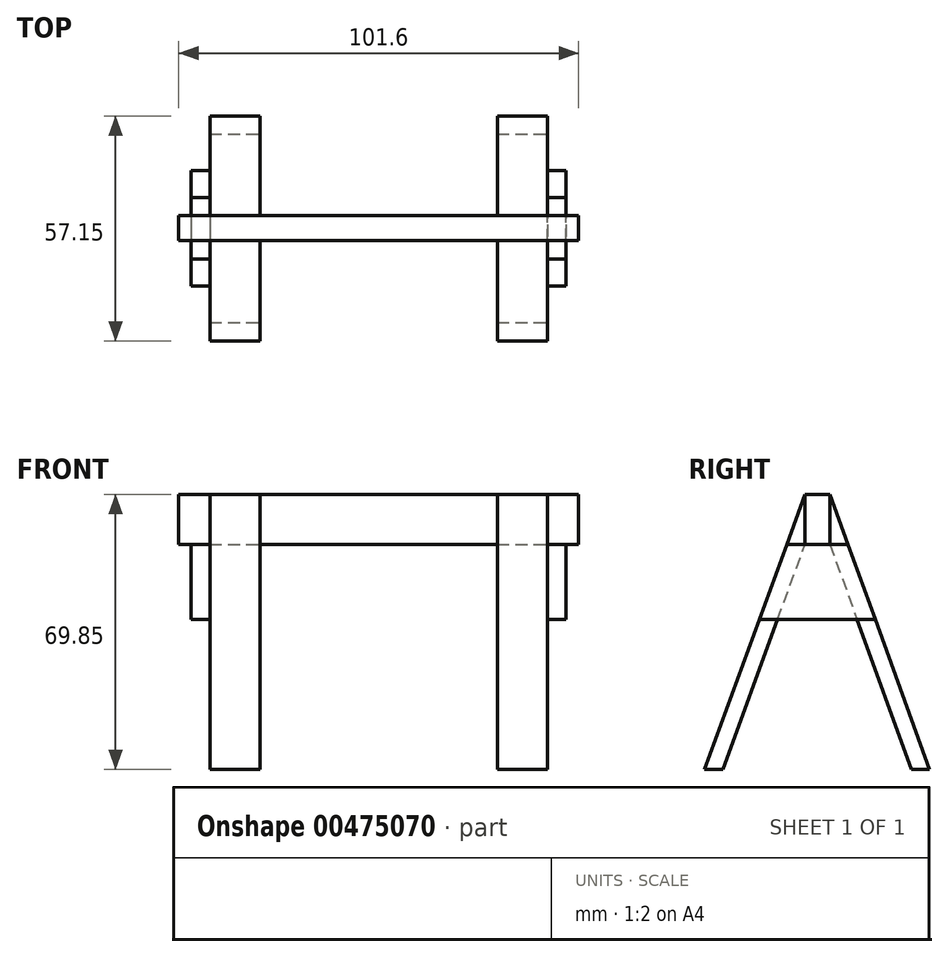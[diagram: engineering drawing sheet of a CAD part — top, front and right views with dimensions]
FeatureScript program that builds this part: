
annotation { "Feature Type Name" : "Feature", "Feature Type Description" : "" }
export const myFeature = defineFeature(function(context is Context, id is Id, definition is map)
    precondition{}
    {
        {
            var Q0;
            Q0=qCreatedBy(makeId("Right.planeOp"),FACE);
            var sketch = newSketch(context, id + "F0", { "sketchPlane" : qUnion([Q0])});
            skLineSegment(sketch, "E0.bottom", {"start": v(-4.7, 33.69) * mm, "end": v(1.65, 33.69) * mm});
            skLineSegment(sketch, "E0.top", {"start": v(-4.7, 20.99) * mm, "end": v(1.65, 20.99) * mm});
            skLineSegment(sketch, "E0.left", {"start": v(-4.7, 33.69) * mm, "end": v(-4.7, 20.99) * mm});
            skLineSegment(sketch, "E0.right", {"start": v(1.65, 33.69) * mm, "end": v(1.65, 20.99) * mm});
            skLineSegment(sketch, "E1", {"start": v(-4.7, 33.69) * mm, "end": v(-30.2, -36.16) * mm});
            skLineSegment(sketch, "E2", {"start": v(-25.57, -36.16) * mm, "end": v(-4.7, 20.99) * mm});
            skLineSegment(sketch, "E3", {"start": v(-30.2, -36.16) * mm, "end": v(-25.57, -36.16) * mm});
            skLineSegment(sketch, "E4", {"start": v(22.34, -36.16) * mm, "end": v(26.94, -36.16) * mm});
            skLineSegment(sketch, "E5", {"start": v(1.65, 20.99) * mm, "end": v(22.34, -36.16) * mm});
            skLineSegment(sketch, "E6", {"start": v(1.65, 33.69) * mm, "end": v(26.94, -36.16) * mm});
            skLineSegment(sketch, "E7", {"start": v(-4.7, 20.99) * mm, "end": v(-9.33, 20.99) * mm});
            skLineSegment(sketch, "E8", {"start": v(1.65, 20.99) * mm, "end": v(6.25, 20.99) * mm});
            skLineSegment(sketch, "E9", {"start": v(6.2, 1.92) * mm, "end": v(13.16, 1.92) * mm});
            skLineSegment(sketch, "E10", {"start": v(6.2, 1.92) * mm, "end": v(-16.3, 1.92) * mm});
            skLineSegment(sketch, "E11", {"start": v(-9.33, 20.99) * mm, "end": v(-16.3, 1.92) * mm});
            skLineSegment(sketch, "E12", {"start": v(6.25, 20.99) * mm, "end": v(13.16, 1.92) * mm});
            skSolve(sketch);
        }
        {
            var Q0;
            Q0=makeQuery(id+"F0.imprint","IMPRINT",FACE,{"disambiguationData":[TD([[makeQuery(id+"F0.imprint","IMPRINT",EDGE,{"derivedFrom":sQuery(id+"F0.wireOp",EDGE,"E0.bottom")}),-1.0]])]});
            extrude(context, id + "F1", {"entities" : qUnion([Q0]), "oppositeDirection" : true, "depth" : 101.6 * mm});
        }
        {
            var Q0;
            {var subQ0=sQuery(id+"F0.wireOp",EDGE,"E3");Q0=makeQuery(id+"F0.imprint","IMPRINT",FACE,{"disambiguationData":[TD([[makeQuery(id+"F0.imprint","IMPRINT",EDGE,{"derivedFrom":subQ0}),1.0]])]});}
            var Q1;
            {var subQ0=sQuery(id+"F0.wireOp",EDGE,"E4");Q1=makeQuery(id+"F0.imprint","IMPRINT",FACE,{"disambiguationData":[TD([[makeQuery(id+"F0.imprint","IMPRINT",EDGE,{"derivedFrom":subQ0}),1.0]])]});}
            var Q2;
            {var subQ0=sQuery(id+"F0.wireOp",EDGE,"E0.left");Q2=makeQuery(id+"F0.imprint","IMPRINT",FACE,{"disambiguationData":[TD([[makeQuery(id+"F0.imprint","IMPRINT",EDGE,{"derivedFrom":subQ0}),-1.0]])]});}
            var Q3;
            {var subQ0=sQuery(id+"F0.wireOp",EDGE,"E0.right");Q3=makeQuery(id+"F0.imprint","IMPRINT",FACE,{"disambiguationData":[TD([[makeQuery(id+"F0.imprint","IMPRINT",EDGE,{"derivedFrom":subQ0}),1.0]])]});}
            var Q4;
            Q4=makeQuery(id+"F0.imprint","IMPRINT",FACE,{"disambiguationData":[TD([[makeQuery(id+"F0.imprint","IMPRINT",EDGE,{"derivedFrom":sQuery(id+"F0.wireOp",EDGE,"E0.bottom")}),-1.0]])]});
            var Q5;
            {var subQ0=sQuery(id+"F0.wireOp",EDGE,"E7");Q5=makeQuery(id+"F0.imprint","IMPRINT",FACE,{"disambiguationData":[TD([[makeQuery(id+"F0.imprint","IMPRINT",EDGE,{"derivedFrom":subQ0}),1.0]])]});}
            var Q6;
            {var subQ0=sQuery(id+"F0.wireOp",EDGE,"E8");Q6=makeQuery(id+"F0.imprint","IMPRINT",FACE,{"disambiguationData":[TD([[makeQuery(id+"F0.imprint","IMPRINT",EDGE,{"derivedFrom":subQ0}),-1.0]])]});}
            extrude(context, id + "F2", {"entities" : qUnion([Q0, Q1, Q2, Q3, Q4, Q5, Q6]), "operationType" : NewBodyOperationType.ADD, "oppositeDirection" : true, "depth" : 20.64 * mm, "hasSecondDirection" : true, "secondDirectionOppositeDirection" : true, "secondDirectionDepth" : 7.94 * mm});
        }
        {
            var Q0;
            {var subQ0=sQuery(id+"F0.wireOp",EDGE,"E3");Q0=makeQuery(id+"F0.imprint","IMPRINT",FACE,{"disambiguationData":[TD([[makeQuery(id+"F0.imprint","IMPRINT",EDGE,{"derivedFrom":subQ0}),1.0]])]});}
            var Q1;
            {var subQ0=sQuery(id+"F0.wireOp",EDGE,"E4");Q1=makeQuery(id+"F0.imprint","IMPRINT",FACE,{"disambiguationData":[TD([[makeQuery(id+"F0.imprint","IMPRINT",EDGE,{"derivedFrom":subQ0}),1.0]])]});}
            var Q2;
            {var subQ0=sQuery(id+"F0.wireOp",EDGE,"E8");Q2=makeQuery(id+"F0.imprint","IMPRINT",FACE,{"disambiguationData":[TD([[makeQuery(id+"F0.imprint","IMPRINT",EDGE,{"derivedFrom":subQ0}),-1.0]])]});}
            var Q3;
            {var subQ0=sQuery(id+"F0.wireOp",EDGE,"E7");Q3=makeQuery(id+"F0.imprint","IMPRINT",FACE,{"disambiguationData":[TD([[makeQuery(id+"F0.imprint","IMPRINT",EDGE,{"derivedFrom":subQ0}),1.0]])]});}
            var Q4;
            {var subQ0=sQuery(id+"F0.wireOp",EDGE,"E0.left");Q4=makeQuery(id+"F0.imprint","IMPRINT",FACE,{"disambiguationData":[TD([[makeQuery(id+"F0.imprint","IMPRINT",EDGE,{"derivedFrom":subQ0}),-1.0]])]});}
            var Q5;
            {var subQ0=sQuery(id+"F0.wireOp",EDGE,"E0.right");Q5=makeQuery(id+"F0.imprint","IMPRINT",FACE,{"disambiguationData":[TD([[makeQuery(id+"F0.imprint","IMPRINT",EDGE,{"derivedFrom":subQ0}),1.0]])]});}
            extrude(context, id + "F3", {"entities" : qUnion([Q0, Q1, Q2, Q3, Q4, Q5]), "operationType" : NewBodyOperationType.ADD, "oppositeDirection" : true, "depth" : 93.66 * mm, "hasSecondDirection" : true, "secondDirectionOppositeDirection" : true, "secondDirectionDepth" : 80.96 * mm});
        }
        {
            var Q0;
            {var subQ0=sQuery(id+"F0.wireOp",EDGE,"E0.top");Q0=makeQuery(id+"F0.imprint","IMPRINT",FACE,{"disambiguationData":[TD([[makeQuery(id+"F0.imprint","IMPRINT",EDGE,{"derivedFrom":subQ0}),-1.0]])]});}
            var Q1;
            {var subQ0=sQuery(id+"F0.wireOp",EDGE,"E7");Q1=makeQuery(id+"F0.imprint","IMPRINT",FACE,{"disambiguationData":[TD([[makeQuery(id+"F0.imprint","IMPRINT",EDGE,{"derivedFrom":subQ0}),1.0]])]});}
            var Q2;
            {var subQ0=sQuery(id+"F0.wireOp",EDGE,"E8");Q2=makeQuery(id+"F0.imprint","IMPRINT",FACE,{"disambiguationData":[TD([[makeQuery(id+"F0.imprint","IMPRINT",EDGE,{"derivedFrom":subQ0}),-1.0]])]});}
            extrude(context, id + "F4", {"entities" : qUnion([Q0, Q1, Q2]), "oppositeDirection" : true, "depth" : 7.95 * mm, "hasSecondDirection" : true, "secondDirectionOppositeDirection" : true, "secondDirectionDepth" : 3.17 * mm});
        }
        {
            var Q0;
            {var subQ0=sQuery(id+"F0.wireOp",EDGE,"E7");Q0=makeQuery(id+"F0.imprint","IMPRINT",FACE,{"disambiguationData":[TD([[makeQuery(id+"F0.imprint","IMPRINT",EDGE,{"derivedFrom":subQ0}),1.0]])]});}
            var Q1;
            {var subQ0=sQuery(id+"F0.wireOp",EDGE,"E0.top");Q1=makeQuery(id+"F0.imprint","IMPRINT",FACE,{"disambiguationData":[TD([[makeQuery(id+"F0.imprint","IMPRINT",EDGE,{"derivedFrom":subQ0}),-1.0]])]});}
            var Q2;
            {var subQ0=sQuery(id+"F0.wireOp",EDGE,"E8");Q2=makeQuery(id+"F0.imprint","IMPRINT",FACE,{"disambiguationData":[TD([[makeQuery(id+"F0.imprint","IMPRINT",EDGE,{"derivedFrom":subQ0}),-1.0]])]});}
            extrude(context, id + "F5", {"entities" : qUnion([Q0, Q1, Q2]), "oppositeDirection" : true, "depth" : 98.42 * mm, "hasSecondDirection" : true, "secondDirectionOppositeDirection" : true, "secondDirectionDepth" : 93.65 * mm});
        }
    });
